# Revit family: Alcon-14001-S-Revit-Family
name_source: partatom
category: Lighting Fixtures
units: mm (PartAtom-declared; Revit-internal decimal feet)

## family parameters
Cut with Voids When Loaded = Yes
Host = Face
Light Source = Yes
Part Type = Normal
Room Calculation Point = No
Round Connector Dimension = Use Diameter
Shared = No

## types (3) — shared parameters
Color Filter = 16777215
Default Elevation = 4' - 0"
Dimming Lamp Color Temperature Shift = <None>
Emit Shape Visible in Rendering = No
Housing = Housing
Lens = Lens
Light Source Symbol Size = 2' - 0"
Link To Product Page = https://www.alconlighting.com
Manufacturer = Alcon Light
Product identity = Alcon lighting 14001-S
URL = https://www.alconlighting.com

## per-type parameters (varying)
| type | Emit from Rectangle Length | Emit from Rectangle Width | Length | Width |
| 2'x2' | 2' - 0" | 2' - 0" | 2' - 0" | 2' - 0" |
| 2'x4' | 2' - 0" | 4' - 0" | 4' - 0" | 2' - 0" |
| 1'x4' | 1' - 0" | 4' - 0" | 4' - 0" | 1' - 0" |

## geometry (parser evidence)
native form markers: Sweep x3
no freeform markers — native parametric forms only
